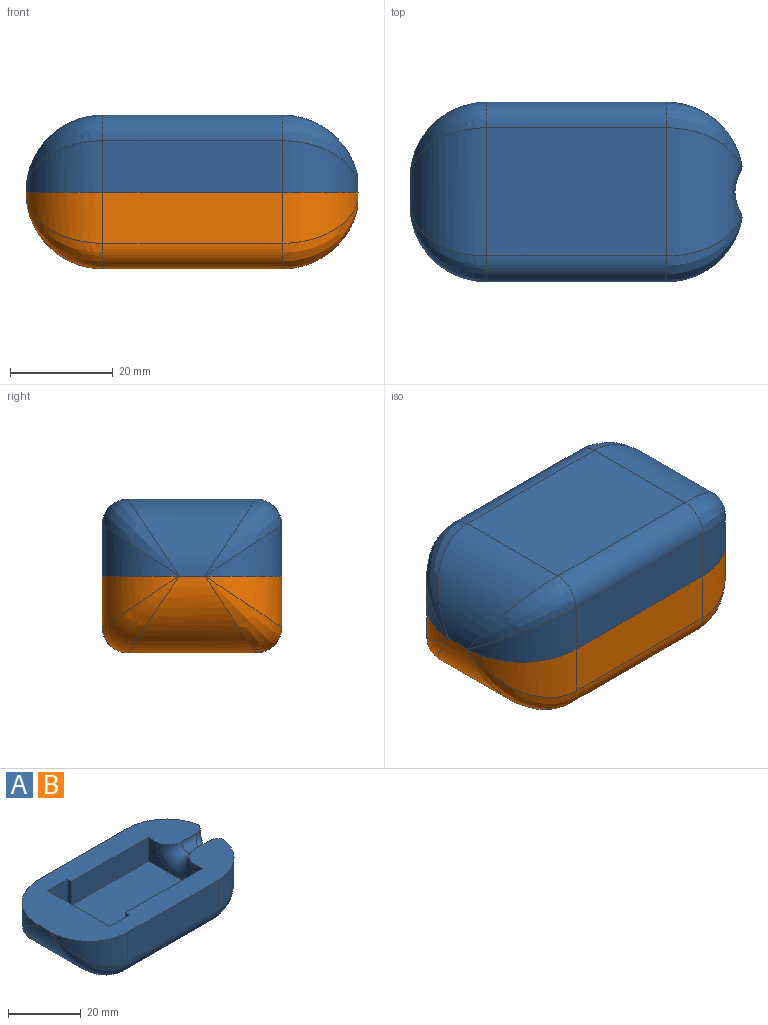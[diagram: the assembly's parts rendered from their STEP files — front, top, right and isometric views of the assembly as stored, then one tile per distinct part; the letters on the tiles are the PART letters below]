
ASSEMBLY  parts=2 mates=1
PART A: 32 faces, bbox 66.1x35.1x15.9 mm
  f0: plane 64.89x35.14mm, normal (0,0,1), area 1184.1mm2, adj f1,f2,f4,f5,f7,f8,f9,f14
  f1: plane 29.77x8mm, normal (0,1,0), area 238.1mm2, adj f0,f3,f19,f23
  f2: plane 29.77x8mm, normal (0,-1,0), area 238.1mm2, adj f0,f3,f19,f23
  f3: plane 29.77x21mm, normal (0,0,1), area 625.1mm2, adj f1,f2,f19,f23
  f4: plane 35x10mm, normal (0,1,0), area 350mm2, adj f0,f9,f13,f18
  f5: plane 35x10mm, normal (0,-1,0), area 350mm2, adj f0,f7,f11,f14
  f6: plane 35x25mm, normal (0,0,-1), area 875mm2, adj f8,f11,f13,f16
  f7: cylinder r=15mm len=15mm, axis (0,0,1), area 117.8mm2, adj f0,f5,f10
  f8: cylinder r=15mm len=25mm, axis (0,-1,0), area 353.4mm2, adj f0,f6,f10,f12
  f9: cylinder r=15mm len=15mm, axis (0,0,-1), area 117.8mm2, adj f0,f4,f12
  f10: bspline ~17.59x15mm, area 81.2mm2, adj f7,f8,f11
  f11: cylinder r=5mm len=35mm, axis (1,0,0), area 274.9mm2, adj f5,f6,f10,f15
  f12: bspline ~17.59x15mm, area 81.2mm2, adj f8,f9,f13
  f13: cylinder r=5mm len=35mm, axis (-1,0,0), area 274.9mm2, adj f4,f6,f12,f17
  f14: cylinder r=15mm len=14.72mm, axis (0,0,-1), area 147.2mm2, adj f0,f5,f15,f29
  f15: bspline ~15.64x14.35mm, area 122.5mm2, adj f11,f14,f16,f28
  f16: cylinder r=15mm len=25mm, axis (0,1,0), area 316.3mm2, adj f6,f15,f17,f22
  f17: bspline ~15.64x14.35mm, area 122.5mm2, adj f13,f16,f18,f31
  f18: cylinder r=15mm len=14.72mm, axis (0,0,1), area 147.2mm2, adj f0,f4,f17,f30
  f19: plane 21x8mm, normal (-1,0,0), area 79.6mm2, adj f0,f1,f2,f3,f21
  f20: cylinder r=2.5mm len=5.72mm, axis (-1,0,0), area 45mm2, adj f0,f21,f22
  f21: torus R=7.5mm, axis (-1,0,0), area 106.5mm2, adj f0,f19,f20
  f22: bspline ~11.81x8.37mm, area 72.6mm2, adj f0,f16,f20,f28,f29,f30,f31
  f23: plane 24x12mm, normal (-1,0,0), area 120mm2, adj f0,f1,f2,f3,f24,f26,f27
  f24: plane 12x7.78mm, normal (0,-1,0), area 93.3mm2, adj f0,f23,f25,f27
  f25: plane 24x12mm, normal (1,0,0), area 288mm2, adj f0,f24,f26,f27
  f26: plane 12x7.78mm, normal (0,1,0), area 93.3mm2, adj f0,f23,f25,f27
  f27: plane 24x7.78mm, normal (0,0,1), area 186.6mm2, adj f23,f24,f25,f26
  f28: bspline ~3.14x1.51mm, area 0.6mm2, adj f15,f22,f29
  f29: bspline ~2.48x1.35mm, area 2.4mm2, adj f0,f14,f22,f28
  f30: bspline ~2.67x1.38mm, area 2.4mm2, adj f0,f18,f22,f31
  f31: bspline ~1.94x0.97mm, area 0.6mm2, adj f17,f22,f30
PART B: same geometry as A
PLACE A rot(axis=(1,0,0),180deg) t=(-13.34,17.38,58.97)mm
PLACE B t=(-13.34,17.38,28.97)mm
MATE fastened A.f0 <-> B.f0  axis (0,0,-1) through (-45.84,17.38,43.97)mm
